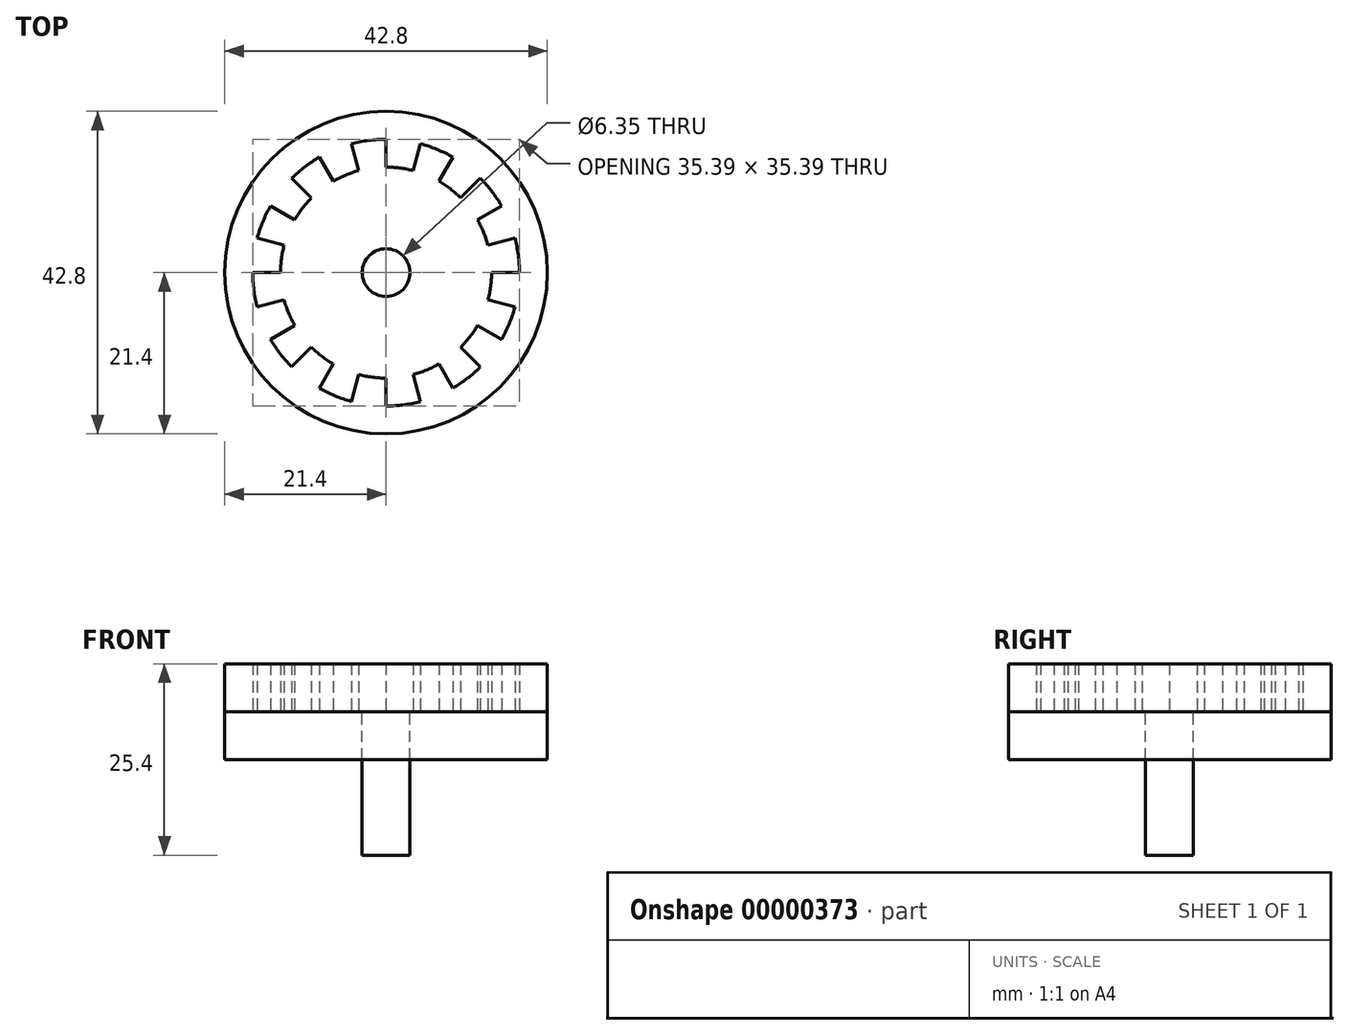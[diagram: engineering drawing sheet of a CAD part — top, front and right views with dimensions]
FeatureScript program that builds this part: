
annotation { "Feature Type Name" : "Feature", "Feature Type Description" : "" }
export const myFeature = defineFeature(function(context is Context, id is Id, definition is map)
    precondition{}
    {
        {
            var Q0;
            Q0=qCreatedBy(makeId("Top.planeOp"),FACE);
            var sketch = newSketch(context, id + "F0", { "sketchPlane" : qUnion([Q0])});
            skCircle(sketch, "E0", {"center": v(0, 0) * mm, "radius": 14 * mm, "construction": true});
            skCircle(sketch, "E1", {"center": v(0, 0) * mm, "radius": 21.4 * mm});
            skCircle(sketch, "E2", {"center": v(0, 0) * mm, "radius": 17.7 * mm});
            skLineSegment(sketch, "E3", {"start": v(9.1, 15.18) * mm, "end": v(6.83, 12.22) * mm, "construction": true});
            skLineSegment(sketch, "E4", {"start": v(9.1, 15.18) * mm, "end": v(11.37, 18.13) * mm, "construction": true});
            skLineSegment(sketch, "E5", {"start": v(0, 0) * mm, "end": v(0, 14) * mm, "construction": true});
            skLineSegment(sketch, "E6", {"start": v(0, 14) * mm, "end": v(0, 17.7) * mm});
            skLineSegment(sketch, "E7", {"start": v(0, 0) * mm, "end": v(3.62, 13.52) * mm, "construction": true});
            skLineSegment(sketch, "E8", {"start": v(3.62, 13.52) * mm, "end": v(4.58, 17.1) * mm});
            skArc(sketch, "E9", {"start": v(3.62, 13.52) * mm, "mid": v(1.83, 13.88) * mm, "end": v(0, 14) * mm});
            skSolve(sketch);
        }
        {
            var Q0;
            Q0=makeQuery(id+"F0.imprint","IMPRINT",FACE,{"disambiguationData":[TD([[makeQuery(id+"F0.imprint","IMPRINT",EDGE,{"derivedFrom":sQuery(id+"F0.wireOp",EDGE,"E1")}),1.0]])]});
            extrude(context, id + "F1", {"entities" : qUnion([Q0]), "depth" : 6.35 * mm});
        }
        {
            var Q0;
            {var subQ1=sQuery(id+"F0.wireOp",EDGE,"E6");Q0=makeQuery(id+"F0.imprint","IMPRINT",FACE,{"disambiguationData":[TD([[makeQuery(id+"F0.imprint","IMPRINT",EDGE,{"derivedFrom":subQ1}),-1.0]])]});}
            extrude(context, id + "F2", {"entities" : qUnion([Q0]), "depth" : 6.35 * mm});
        }
        {
            var Q0;
            Q0=qCreatedBy(makeId("Front.planeOp"),FACE);
            var sketch = newSketch(context, id + "F3", { "sketchPlane" : qUnion([Q0])});
            skLineSegment(sketch, "E10", {"start": v(0, 0) * mm, "end": v(0, 20.1) * mm, "construction": true});
            skSolve(sketch);
        }
        {
            var Q0;
            Q0=makeQuery(id+"F2.opExtrude","SWEPT_BODY",BODY,{"disambiguationData":[OSD([sQuery(id+"F0.wireOp",EDGE,"E2"),sQuery(id+"F0.wireOp",EDGE,"E6"),sQuery(id+"F0.wireOp",EDGE,"E8"),sQuery(id+"F0.wireOp",EDGE,"E9")])]});
            var Q1;
            Q1=sQuery(id+"F3.wireOp",EDGE,"E10");
            circularPattern(context, id + "F4", {"entities" : qUnion([Q0]), "axis" : qUnion([Q1]), "angle" : 30 * degree, "instanceCount" : 12});
        }
        {
            var Q0;
            Q0=qCreatedBy(makeId("Top.planeOp"),FACE);
            var sketch = newSketch(context, id + "F5", { "sketchPlane" : qUnion([Q0])});
            skCircle(sketch, "E11", {"center": v(0, 0) * mm, "radius": 21.4 * mm});
            skCircle(sketch, "E12", {"center": v(0, 0) * mm, "radius": 3.18 * mm});
            skSolve(sketch);
        }
        {
            var Q0;
            Q0=makeQuery(id+"F5.imprint","IMPRINT",FACE,{"disambiguationData":[TD([[makeQuery(id+"F5.imprint","IMPRINT",EDGE,{"derivedFrom":sQuery(id+"F5.wireOp",EDGE,"E11")}),1.0]])]});
            extrude(context, id + "F6", {"entities" : qUnion([Q0]), "oppositeDirection" : true, "depth" : 6.35 * mm});
        }
        {
            var Q0;
            Q0=makeQuery(id+"F1.opExtrude","SWEPT_BODY",BODY,{"disambiguationData":[OSD([sQuery(id+"F0.wireOp",EDGE,"E1"),sQuery(id+"F0.wireOp",EDGE,"E2")])]});
            var Q1;
            Q1=makeQuery(id+"F2.opExtrude","SWEPT_BODY",BODY,{"disambiguationData":[OSD([sQuery(id+"F0.wireOp",EDGE,"E2"),sQuery(id+"F0.wireOp",EDGE,"E6"),sQuery(id+"F0.wireOp",EDGE,"E8"),sQuery(id+"F0.wireOp",EDGE,"E9")])]});
            var Q2;
            Q2=makeQuery(id+"F4.opPattern","COPY",BODY,{"derivedFrom":makeQuery(id+"F2.opExtrude","SWEPT_BODY",BODY,{"disambiguationData":[OSD([sQuery(id+"F0.wireOp",EDGE,"E2"),sQuery(id+"F0.wireOp",EDGE,"E6"),sQuery(id+"F0.wireOp",EDGE,"E8"),sQuery(id+"F0.wireOp",EDGE,"E9")])]}),"instanceName":"1"});
            var Q3;
            Q3=makeQuery(id+"F4.opPattern","COPY",BODY,{"derivedFrom":makeQuery(id+"F2.opExtrude","SWEPT_BODY",BODY,{"disambiguationData":[OSD([sQuery(id+"F0.wireOp",EDGE,"E2"),sQuery(id+"F0.wireOp",EDGE,"E6"),sQuery(id+"F0.wireOp",EDGE,"E8"),sQuery(id+"F0.wireOp",EDGE,"E9")])]}),"instanceName":"2"});
            var Q4;
            Q4=makeQuery(id+"F4.opPattern","COPY",BODY,{"derivedFrom":makeQuery(id+"F2.opExtrude","SWEPT_BODY",BODY,{"disambiguationData":[OSD([sQuery(id+"F0.wireOp",EDGE,"E2"),sQuery(id+"F0.wireOp",EDGE,"E6"),sQuery(id+"F0.wireOp",EDGE,"E8"),sQuery(id+"F0.wireOp",EDGE,"E9")])]}),"instanceName":"3"});
            var Q5;
            Q5=makeQuery(id+"F4.opPattern","COPY",BODY,{"derivedFrom":makeQuery(id+"F2.opExtrude","SWEPT_BODY",BODY,{"disambiguationData":[OSD([sQuery(id+"F0.wireOp",EDGE,"E2"),sQuery(id+"F0.wireOp",EDGE,"E6"),sQuery(id+"F0.wireOp",EDGE,"E8"),sQuery(id+"F0.wireOp",EDGE,"E9")])]}),"instanceName":"4"});
            var Q6;
            Q6=makeQuery(id+"F4.opPattern","COPY",BODY,{"derivedFrom":makeQuery(id+"F2.opExtrude","SWEPT_BODY",BODY,{"disambiguationData":[OSD([sQuery(id+"F0.wireOp",EDGE,"E2"),sQuery(id+"F0.wireOp",EDGE,"E6"),sQuery(id+"F0.wireOp",EDGE,"E8"),sQuery(id+"F0.wireOp",EDGE,"E9")])]}),"instanceName":"5"});
            var Q7;
            Q7=makeQuery(id+"F4.opPattern","COPY",BODY,{"derivedFrom":makeQuery(id+"F2.opExtrude","SWEPT_BODY",BODY,{"disambiguationData":[OSD([sQuery(id+"F0.wireOp",EDGE,"E2"),sQuery(id+"F0.wireOp",EDGE,"E6"),sQuery(id+"F0.wireOp",EDGE,"E8"),sQuery(id+"F0.wireOp",EDGE,"E9")])]}),"instanceName":"6"});
            var Q8;
            Q8=makeQuery(id+"F4.opPattern","COPY",BODY,{"derivedFrom":makeQuery(id+"F2.opExtrude","SWEPT_BODY",BODY,{"disambiguationData":[OSD([sQuery(id+"F0.wireOp",EDGE,"E2"),sQuery(id+"F0.wireOp",EDGE,"E6"),sQuery(id+"F0.wireOp",EDGE,"E8"),sQuery(id+"F0.wireOp",EDGE,"E9")])]}),"instanceName":"7"});
            var Q9;
            Q9=makeQuery(id+"F4.opPattern","COPY",BODY,{"derivedFrom":makeQuery(id+"F2.opExtrude","SWEPT_BODY",BODY,{"disambiguationData":[OSD([sQuery(id+"F0.wireOp",EDGE,"E2"),sQuery(id+"F0.wireOp",EDGE,"E6"),sQuery(id+"F0.wireOp",EDGE,"E8"),sQuery(id+"F0.wireOp",EDGE,"E9")])]}),"instanceName":"8"});
            var Q10;
            Q10=makeQuery(id+"F4.opPattern","COPY",BODY,{"derivedFrom":makeQuery(id+"F2.opExtrude","SWEPT_BODY",BODY,{"disambiguationData":[OSD([sQuery(id+"F0.wireOp",EDGE,"E2"),sQuery(id+"F0.wireOp",EDGE,"E6"),sQuery(id+"F0.wireOp",EDGE,"E8"),sQuery(id+"F0.wireOp",EDGE,"E9")])]}),"instanceName":"9"});
            var Q11;
            Q11=makeQuery(id+"F4.opPattern","COPY",BODY,{"derivedFrom":makeQuery(id+"F2.opExtrude","SWEPT_BODY",BODY,{"disambiguationData":[OSD([sQuery(id+"F0.wireOp",EDGE,"E2"),sQuery(id+"F0.wireOp",EDGE,"E6"),sQuery(id+"F0.wireOp",EDGE,"E8"),sQuery(id+"F0.wireOp",EDGE,"E9")])]}),"instanceName":"10"});
            var Q12;
            Q12=makeQuery(id+"F4.opPattern","COPY",BODY,{"derivedFrom":makeQuery(id+"F2.opExtrude","SWEPT_BODY",BODY,{"disambiguationData":[OSD([sQuery(id+"F0.wireOp",EDGE,"E2"),sQuery(id+"F0.wireOp",EDGE,"E6"),sQuery(id+"F0.wireOp",EDGE,"E8"),sQuery(id+"F0.wireOp",EDGE,"E9")])]}),"instanceName":"11"});
            booleanBodies(context, id + "F7", {"operationType" : BooleanOperationType.UNION, "tools" : qUnion([Q0, Q1, Q2, Q3, Q4, Q5, Q6, Q7, Q8, Q9, Q10, Q11, Q12])});
        }
        {
            var Q0;
            Q0=makeQuery(id+"F0.imprint","IMPRINT",FACE,{"disambiguationData":[TD([[makeQuery(id+"F0.imprint","IMPRINT",EDGE,{"derivedFrom":sQuery(id+"F0.wireOp",EDGE,"E1")}),1.0]])]});
            var sketch = newSketch(context, id + "F8", { "sketchPlane" : qUnion([Q0])});
            skCircle(sketch, "E13", {"center": v(0, 0) * mm, "radius": 3.18 * mm});
            skSolve(sketch);
        }
        {
            var Q0;
            Q0=makeQuery(id+"F8.imprint","IMPRINT",FACE,{"disambiguationData":[TD([[makeQuery(id+"F8.imprint","IMPRINT",EDGE,{"derivedFrom":sQuery(id+"F8.wireOp",EDGE,"E13")}),1.0]])]});
            extrude(context, id + "F9", {"entities" : qUnion([Q0]), "oppositeDirection" : true, "depth" : 19.05 * mm});
        }
    });
